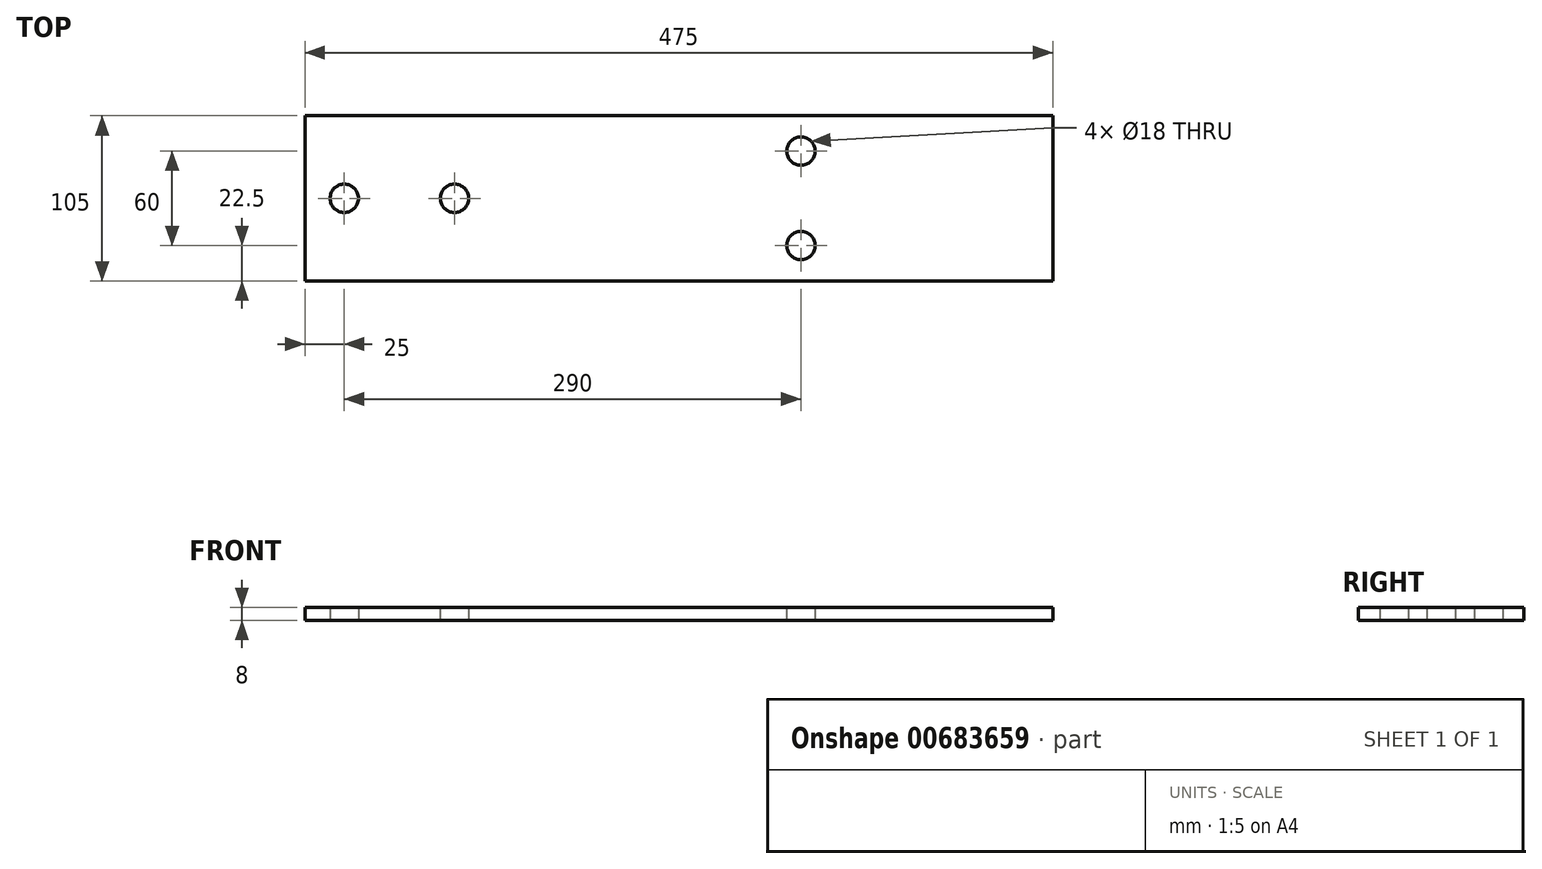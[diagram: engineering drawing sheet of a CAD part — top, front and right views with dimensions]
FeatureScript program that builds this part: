
annotation { "Feature Type Name" : "Feature", "Feature Type Description" : "" }
export const myFeature = defineFeature(function(context is Context, id is Id, definition is map)
    precondition{}
    {
        {
            var Q0;
            Q0=qCreatedBy(makeId("Top.planeOp"),FACE);
            var sketch = newSketch(context, id + "F0", { "sketchPlane" : qUnion([Q0])});
            skLineSegment(sketch, "E0.bottom", {"start": v(0, 0) * mm, "end": v(475, 0) * mm});
            skLineSegment(sketch, "E0.top", {"start": v(0, 105) * mm, "end": v(475, 105) * mm});
            skLineSegment(sketch, "E0.left", {"start": v(0, 0) * mm, "end": v(0, 105) * mm});
            skLineSegment(sketch, "E0.right", {"start": v(475, 0) * mm, "end": v(475, 105) * mm});
            skCircle(sketch, "E1", {"center": v(25, 52.5) * mm, "radius": 9 * mm});
            skPoint(sketch, "E1.centerSnap0", {"position": v(0, 52.5) * mm});
            skCircle(sketch, "E2", {"center": v(95, 52.5) * mm, "radius": 9 * mm});
            skCircle(sketch, "E3", {"center": v(315, 82.5) * mm, "radius": 9 * mm});
            skCircle(sketch, "E4", {"center": v(315, 22.5) * mm, "radius": 9 * mm});
            skSolve(sketch);
        }
        {
            var Q0;
            Q0=makeQuery(id+"F0.imprint","IMPRINT",FACE,{"disambiguationData":[TD([[makeQuery(id+"F0.imprint","IMPRINT",EDGE,{"derivedFrom":sQuery(id+"F0.wireOp",EDGE,"E0.bottom")}),1.0]])]});
            extrude(context, id + "F1", {"entities" : qUnion([Q0]), "depth" : 8 * mm, "offsetDistance" : 25 * mm});
        }
    });
